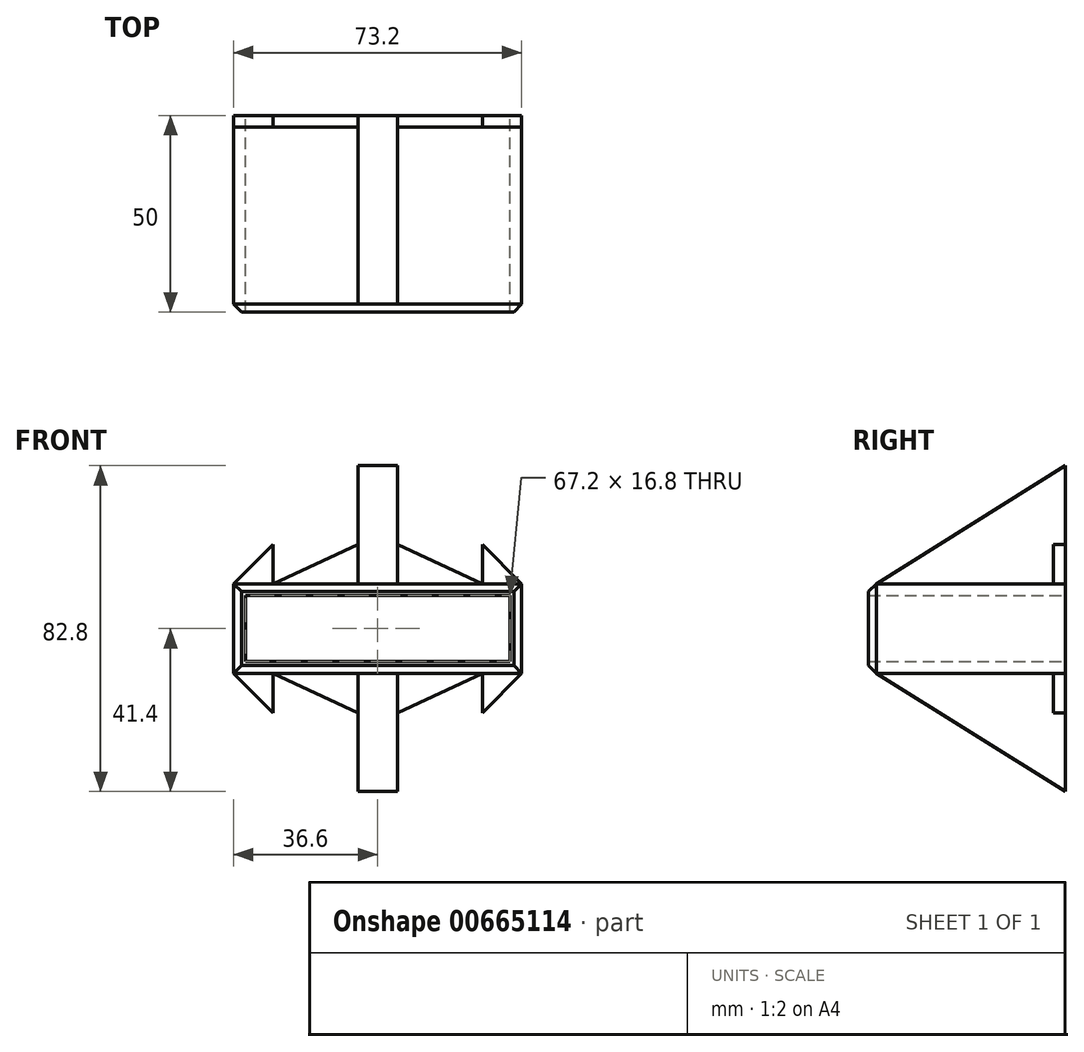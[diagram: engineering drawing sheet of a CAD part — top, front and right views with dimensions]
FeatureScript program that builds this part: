
annotation { "Feature Type Name" : "Feature", "Feature Type Description" : "" }
export const myFeature = defineFeature(function(context is Context, id is Id, definition is map)
    precondition{}
    {
        {
            var Q0;
            Q0=qCreatedBy(makeId("Front.planeOp"),FACE);
            var sketch = newSketch(context, id + "F0", { "sketchPlane" : qUnion([Q0])});
            skLineSegment(sketch, "E0.bottom", {"start": v(-33.6, -8.4) * mm, "end": v(33.6, -8.4) * mm});
            skLineSegment(sketch, "E0.top", {"start": v(-33.6, 8.4) * mm, "end": v(33.6, 8.4) * mm});
            skLineSegment(sketch, "E0.left", {"start": v(-33.6, -8.4) * mm, "end": v(-33.6, 8.4) * mm});
            skLineSegment(sketch, "E0.right", {"start": v(33.6, -8.4) * mm, "end": v(33.6, 8.4) * mm});
            skPoint(sketch, "E0.middle", {"position": v(0, 0) * mm});
            skLineSegment(sketch, "E1.0", {"start": v(-36.6, -11.4) * mm, "end": v(-36.6, 11.4) * mm});
            skLineSegment(sketch, "E1.1", {"start": v(-36.6, -11.4) * mm, "end": v(36.6, -11.4) * mm});
            skLineSegment(sketch, "E1.2", {"start": v(36.6, -11.4) * mm, "end": v(36.6, 11.4) * mm});
            skLineSegment(sketch, "E1.3", {"start": v(-36.6, 11.4) * mm, "end": v(36.6, 11.4) * mm});
            skSolve(sketch);
        }
        {
            var Q0;
            Q0=makeQuery(id+"F0.imprint","IMPRINT",FACE,{"disambiguationData":[TD([[makeQuery(id+"F0.imprint","IMPRINT",EDGE,{"derivedFrom":sQuery(id+"F0.wireOp",EDGE,"E0.bottom")}),-1.0]])]});
            extrude(context, id + "F1", {"entities" : qUnion([Q0]), "depth" : 50 * mm, "offsetDistance" : 25 * mm});
        }
        {
            var Q0;
            Q0=makeQuery(id+"F1.opExtrude","CAP_EDGE",EDGE,{"disambiguationData":[OSD([sQuery(id+"F0.wireOp",EDGE,"E1.0")])],"isStart":false});
            var Q1;
            Q1=makeQuery(id+"F1.opExtrude","CAP_EDGE",EDGE,{"disambiguationData":[OSD([sQuery(id+"F0.wireOp",EDGE,"E1.3")])],"isStart":false});
            var Q2;
            Q2=makeQuery(id+"F1.opExtrude","CAP_EDGE",EDGE,{"disambiguationData":[OSD([sQuery(id+"F0.wireOp",EDGE,"E1.2")])],"isStart":false});
            var Q3;
            Q3=makeQuery(id+"F1.opExtrude","CAP_EDGE",EDGE,{"disambiguationData":[OSD([sQuery(id+"F0.wireOp",EDGE,"E1.1")])],"isStart":false});
            chamfer(context, id + "F2", {"entities" : qUnion([Q0, Q1, Q2, Q3]), "width" : 2 * mm, "tangentPropagation" : true});
        }
        {
            var Q0;
            Q0=makeQuery(id+"F1.opExtrude","SWEPT_FACE",FACE,{"disambiguationData":[OSD([sQuery(id+"F0.wireOp",EDGE,"E1.1")])]});
            var sketch = newSketch(context, id + "F3", { "sketchPlane" : qUnion([Q0])});
            skLineSegment(sketch, "E2.0", {"start": v(5, 0) * mm, "end": v(5, 48) * mm});
            skLineSegment(sketch, "E3.0", {"start": v(-5, 0) * mm, "end": v(-5, 48) * mm});
            skSolve(sketch);
        }
        {
            var Q0;
            {var subQ0=sQuery(id+"F3.wireOp",EDGE,"E2.0");Q0=makeQuery(id+"F3.imprint","IMPRINT",FACE,{"disambiguationData":[TD([[makeQuery(id+"F3.imprint","IMPRINT",EDGE,{"derivedFrom":subQ0}),1.0]])]});}
            extrude(context, id + "F4", {"entities" : qUnion([Q0]), "operationType" : NewBodyOperationType.ADD, "depth" : 30 * mm, "offsetDistance" : 25 * mm});
        }
        {
            var Q0;
            Q0=makeQuery(id+"F4.opExtrude","SWEPT_FACE",FACE,{"disambiguationData":[OSD([sQuery(id+"F3.wireOp",EDGE,"E3.0")])]});
            var sketch = newSketch(context, id + "F5", { "sketchPlane" : qUnion([Q0])});
            skLineSegment(sketch, "E4", {"start": v(48, -11.4) * mm, "end": v(0, -41.4) * mm});
            skSolve(sketch);
        }
        {
            var Q0;
            Q0=makeQuery(id+"F5.imprint","IMPRINT",FACE,{"disambiguationData":[TD([[makeQuery(id+"F5.imprint","IMPRINT",EDGE,{"derivedFrom":sQuery(id+"F5.wireOp",EDGE,"E4")}),1.0]])]});
            extrude(context, id + "F6", {"entities" : qUnion([Q0]), "operationType" : NewBodyOperationType.REMOVE, "oppositeDirection" : true, "depth" : 25 * mm, "offsetDistance" : 25 * mm});
        }
        {
            var Q0;
            Q0=makeQuery(id+"F1.opExtrude","SWEPT_FACE",FACE,{"disambiguationData":[OSD([sQuery(id+"F0.wireOp",EDGE,"E1.3")])]});
            var sketch = newSketch(context, id + "F7", { "sketchPlane" : qUnion([Q0])});
            skLineSegment(sketch, "E5.0", {"start": v(-5, 0) * mm, "end": v(-5, -48) * mm});
            skLineSegment(sketch, "E6.0", {"start": v(5, 0) * mm, "end": v(5, -48) * mm});
            skSolve(sketch);
        }
        {
            var Q0;
            {var subQ0=sQuery(id+"F7.wireOp",EDGE,"E5.0");Q0=makeQuery(id+"F7.imprint","IMPRINT",FACE,{"disambiguationData":[TD([[makeQuery(id+"F7.imprint","IMPRINT",EDGE,{"derivedFrom":subQ0}),1.0]])]});}
            extrude(context, id + "F8", {"entities" : qUnion([Q0]), "operationType" : NewBodyOperationType.ADD, "depth" : 30 * mm, "offsetDistance" : 25 * mm});
        }
        {
            var Q0;
            Q0=makeQuery(id+"F8.opExtrude","SWEPT_FACE",FACE,{"disambiguationData":[OSD([sQuery(id+"F7.wireOp",EDGE,"E6.0")])]});
            var sketch = newSketch(context, id + "F9", { "sketchPlane" : qUnion([Q0])});
            skLineSegment(sketch, "E7", {"start": v(-48, 11.4) * mm, "end": v(0, 41.4) * mm});
            skSolve(sketch);
        }
        {
            var Q0;
            Q0=makeQuery(id+"F9.imprint","IMPRINT",FACE,{"disambiguationData":[TD([[makeQuery(id+"F9.imprint","IMPRINT",EDGE,{"derivedFrom":sQuery(id+"F9.wireOp",EDGE,"E7")}),1.0]])]});
            extrude(context, id + "F10", {"entities" : qUnion([Q0]), "operationType" : NewBodyOperationType.REMOVE, "oppositeDirection" : true, "depth" : 25 * mm, "offsetDistance" : 25 * mm});
        }
        {
            var Q0;
            {var subQ0=sQuery(id+"F0.wireOp",EDGE,"E1.3");var subQ1=sQuery(id+"F0.wireOp",EDGE,"E1.0");var subQ5=makeQuery(id+"F1.opExtrude","SWEPT_FACE",FACE,{"disambiguationData":[OSD([subQ0])]});Q0=makeQuery(id+"F8.boolean.opBoolean","SPLIT",FACE,{"disambiguationData":[TD([makeQuery(id+"F1.opExtrude","SWEPT_FACE",FACE,{"disambiguationData":[OSD([subQ1])]})])],"derivedFrom":subQ5});}
            var sketch = newSketch(context, id + "F11", { "sketchPlane" : qUnion([Q0])});
            skLineSegment(sketch, "E8.0", {"start": v(-36.6, -3) * mm, "end": v(-5, -3) * mm});
            skSolve(sketch);
        }
        {
            var Q0;
            {var subQ0=sQuery(id+"F0.wireOp",EDGE,"E1.3");var subQ2=sQuery(id+"F0.wireOp",EDGE,"E1.2");var subQ7=makeQuery(id+"F1.opExtrude","SWEPT_FACE",FACE,{"disambiguationData":[OSD([subQ0])]});Q0=makeQuery(id+"F8.boolean.opBoolean","SPLIT",FACE,{"disambiguationData":[TD([makeQuery(id+"F1.opExtrude","SWEPT_FACE",FACE,{"disambiguationData":[OSD([subQ2])]})])],"derivedFrom":subQ7});}
            var sketch = newSketch(context, id + "F12", { "sketchPlane" : qUnion([Q0])});
            skLineSegment(sketch, "E9.0", {"start": v(5, -3) * mm, "end": v(36.6, -3) * mm});
            skSolve(sketch);
        }
        {
            var Q0;
            {var subQ0=sQuery(id+"F11.wireOp",EDGE,"E8.0");Q0=makeQuery(id+"F11.imprint","IMPRINT",FACE,{"disambiguationData":[TD([[makeQuery(id+"F11.imprint","IMPRINT",EDGE,{"derivedFrom":subQ0}),1.0]])]});}
            var Q1;
            {var subQ0=sQuery(id+"F12.wireOp",EDGE,"E9.0");Q1=makeQuery(id+"F12.imprint","IMPRINT",FACE,{"disambiguationData":[TD([[makeQuery(id+"F12.imprint","IMPRINT",EDGE,{"derivedFrom":subQ0}),1.0]])]});}
            extrude(context, id + "F13", {"entities" : qUnion([Q0, Q1]), "operationType" : NewBodyOperationType.ADD, "depth" : 10 * mm, "offsetDistance" : 25 * mm});
        }
        {
            var Q0;
            Q0=makeQuery(id+"F13.opExtrude","CAP_EDGE",EDGE,{"disambiguationData":[OSD([sQuery(id+"F0.wireOp",EDGE,"E1.2"),sQuery(id+"F0.wireOp",EDGE,"E1.3")])],"isStart":false});
            var Q1;
            Q1=makeQuery(id+"F13.opExtrude","CAP_EDGE",EDGE,{"disambiguationData":[OSD([sQuery(id+"F0.wireOp",EDGE,"E1.0"),sQuery(id+"F0.wireOp",EDGE,"E1.3")])],"isStart":false});
            chamfer(context, id + "F14", {"entities" : qUnion([Q0, Q1]), "width" : 10 * mm, "tangentPropagation" : true});
        }
        {
            var Q0;
            Q0=makeQuery(id+"F13.opExtrude","SWEPT_FACE",FACE,{"disambiguationData":[OSD([sQuery(id+"F11.wireOp",EDGE,"E8.0")])]});
            var sketch = newSketch(context, id + "F15", { "sketchPlane" : qUnion([Q0])});
            skLineSegment(sketch, "E10", {"start": v(-5, 11.4) * mm, "end": v(-26.6, 21.4) * mm});
            skLineSegment(sketch, "E11", {"start": v(-26.6, 21.4) * mm, "end": v(-26.6, 11.4) * mm});
            skLineSegment(sketch, "E12", {"start": v(-26.6, 11.4) * mm, "end": v(-5, 21.4) * mm});
            skCircle(sketch, "E13", {"center": v(-15.8, 16.4) * mm, "radius": 1.5 * mm});
            skSolve(sketch);
        }
        {
            var Q0;
            {var subQ0=sQuery(id+"F15.wireOp",EDGE,"E12");var subQ1=sQuery(id+"F15.wireOp",EDGE,"E10");var subQ2=makeQuery(id+"F15.imprint","INTERSECT",VERTEX,{"derivedFrom":[subQ1,subQ0]});Q0=makeQuery(id+"F15.imprint","IMPRINT",FACE,{"disambiguationData":[TD([[makeQuery(id+"F15.imprint","IMPRINT",EDGE,{"disambiguationData":[TD([[subQ2,-1.0]])],"derivedFrom":subQ1}),1.0]])]});}
            var Q1;
            {var subQ0=sQuery(id+"F15.wireOp",EDGE,"E12");var subQ1=sQuery(id+"F15.wireOp",EDGE,"E10");var subQ2=makeQuery(id+"F15.imprint","INTERSECT",VERTEX,{"derivedFrom":[subQ1,subQ0]});Q1=makeQuery(id+"F15.imprint","IMPRINT",FACE,{"disambiguationData":[TD([[makeQuery(id+"F15.imprint","IMPRINT",EDGE,{"disambiguationData":[TD([[subQ2,-1.0]])],"derivedFrom":subQ1}),-1.0]])]});}
            var Q2;
            {var subQ0=sQuery(id+"F15.wireOp",EDGE,"E13");var subQ1=sQuery(id+"F15.wireOp",EDGE,"E10");var subQ2=makeQuery(id+"F15.imprint","INTERSECT",VERTEX,{"disambiguationData":[OD(0.0)],"derivedFrom":[subQ1,subQ0]});Q2=makeQuery(id+"F15.imprint","IMPRINT",FACE,{"disambiguationData":[TD([[makeQuery(id+"F15.imprint","IMPRINT",EDGE,{"disambiguationData":[TD([[subQ2,-1.0]])],"derivedFrom":subQ1}),-1.0]])]});}
            var Q3;
            {var subQ0=sQuery(id+"F15.wireOp",EDGE,"E13");var subQ1=sQuery(id+"F15.wireOp",EDGE,"E10");var subQ2=makeQuery(id+"F15.imprint","INTERSECT",VERTEX,{"disambiguationData":[OD(0.0)],"derivedFrom":[subQ1,subQ0]});Q3=makeQuery(id+"F15.imprint","IMPRINT",FACE,{"disambiguationData":[TD([[makeQuery(id+"F15.imprint","IMPRINT",EDGE,{"disambiguationData":[TD([[subQ2,-1.0]])],"derivedFrom":subQ1}),1.0]])]});}
            extrude(context, id + "F16", {"entities" : qUnion([Q0, Q1, Q2, Q3]), "operationType" : NewBodyOperationType.REMOVE, "oppositeDirection" : true, "depth" : 25 * mm, "offsetDistance" : 25 * mm});
        }
        {
            var Q0;
            Q0=makeQuery(id+"F13.opExtrude","SWEPT_FACE",FACE,{"disambiguationData":[OSD([sQuery(id+"F12.wireOp",EDGE,"E9.0")])]});
            var sketch = newSketch(context, id + "F17", { "sketchPlane" : qUnion([Q0])});
            skLineSegment(sketch, "E14", {"start": v(5, 11.4) * mm, "end": v(26.6, 21.4) * mm});
            skLineSegment(sketch, "E15", {"start": v(26.6, 21.4) * mm, "end": v(26.6, 11.4) * mm});
            skLineSegment(sketch, "E16", {"start": v(26.6, 11.4) * mm, "end": v(5, 21.4) * mm});
            skCircle(sketch, "E17", {"center": v(15.8, 16.4) * mm, "radius": 1.5 * mm});
            skSolve(sketch);
        }
        {
            var Q0;
            {var subQ0=sQuery(id+"F17.wireOp",EDGE,"E16");var subQ1=sQuery(id+"F17.wireOp",EDGE,"E14");var subQ2=makeQuery(id+"F17.imprint","INTERSECT",VERTEX,{"derivedFrom":[subQ1,subQ0]});Q0=makeQuery(id+"F17.imprint","IMPRINT",FACE,{"disambiguationData":[TD([[makeQuery(id+"F17.imprint","IMPRINT",EDGE,{"disambiguationData":[TD([[subQ2,-1.0]])],"derivedFrom":subQ1}),1.0]])]});}
            var Q1;
            {var subQ0=sQuery(id+"F17.wireOp",EDGE,"E16");var subQ1=sQuery(id+"F17.wireOp",EDGE,"E14");var subQ2=makeQuery(id+"F17.imprint","INTERSECT",VERTEX,{"derivedFrom":[subQ1,subQ0]});Q1=makeQuery(id+"F17.imprint","IMPRINT",FACE,{"disambiguationData":[TD([[makeQuery(id+"F17.imprint","IMPRINT",EDGE,{"disambiguationData":[TD([[subQ2,-1.0]])],"derivedFrom":subQ1}),-1.0]])]});}
            var Q2;
            {var subQ0=sQuery(id+"F17.wireOp",EDGE,"E17");var subQ1=sQuery(id+"F17.wireOp",EDGE,"E14");var subQ2=makeQuery(id+"F17.imprint","INTERSECT",VERTEX,{"disambiguationData":[OD(0.0)],"derivedFrom":[subQ1,subQ0]});Q2=makeQuery(id+"F17.imprint","IMPRINT",FACE,{"disambiguationData":[TD([[makeQuery(id+"F17.imprint","IMPRINT",EDGE,{"disambiguationData":[TD([[subQ2,-1.0]])],"derivedFrom":subQ1}),-1.0]])]});}
            var Q3;
            {var subQ0=sQuery(id+"F17.wireOp",EDGE,"E17");var subQ1=sQuery(id+"F17.wireOp",EDGE,"E14");var subQ2=makeQuery(id+"F17.imprint","INTERSECT",VERTEX,{"disambiguationData":[OD(0.0)],"derivedFrom":[subQ1,subQ0]});Q3=makeQuery(id+"F17.imprint","IMPRINT",FACE,{"disambiguationData":[TD([[makeQuery(id+"F17.imprint","IMPRINT",EDGE,{"disambiguationData":[TD([[subQ2,-1.0]])],"derivedFrom":subQ1}),1.0]])]});}
            extrude(context, id + "F18", {"entities" : qUnion([Q0, Q1, Q2, Q3]), "operationType" : NewBodyOperationType.REMOVE, "oppositeDirection" : true, "depth" : 25 * mm, "offsetDistance" : 25 * mm});
        }
        {
            var Q0;
            Q0=makeQuery(id+"F1.opExtrude","SWEPT_BODY",BODY,{"disambiguationData":[OSD([sQuery(id+"F0.wireOp",EDGE,"E0.bottom"),sQuery(id+"F0.wireOp",EDGE,"E0.top"),sQuery(id+"F0.wireOp",EDGE,"E0.left"),sQuery(id+"F0.wireOp",EDGE,"E0.right"),sQuery(id+"F0.wireOp",EDGE,"E1.0"),sQuery(id+"F0.wireOp",EDGE,"E1.1"),sQuery(id+"F0.wireOp",EDGE,"E1.2"),sQuery(id+"F0.wireOp",EDGE,"E1.3")])]});
            var Q1;
            Q1=qCreatedBy(makeId("Top.planeOp"),FACE);
            mirror(context, id + "F19", {"operationType" : NewBodyOperationType.ADD, "entities" : qUnion([Q0]), "mirrorPlane" : qUnion([Q1])});
        }
    });
